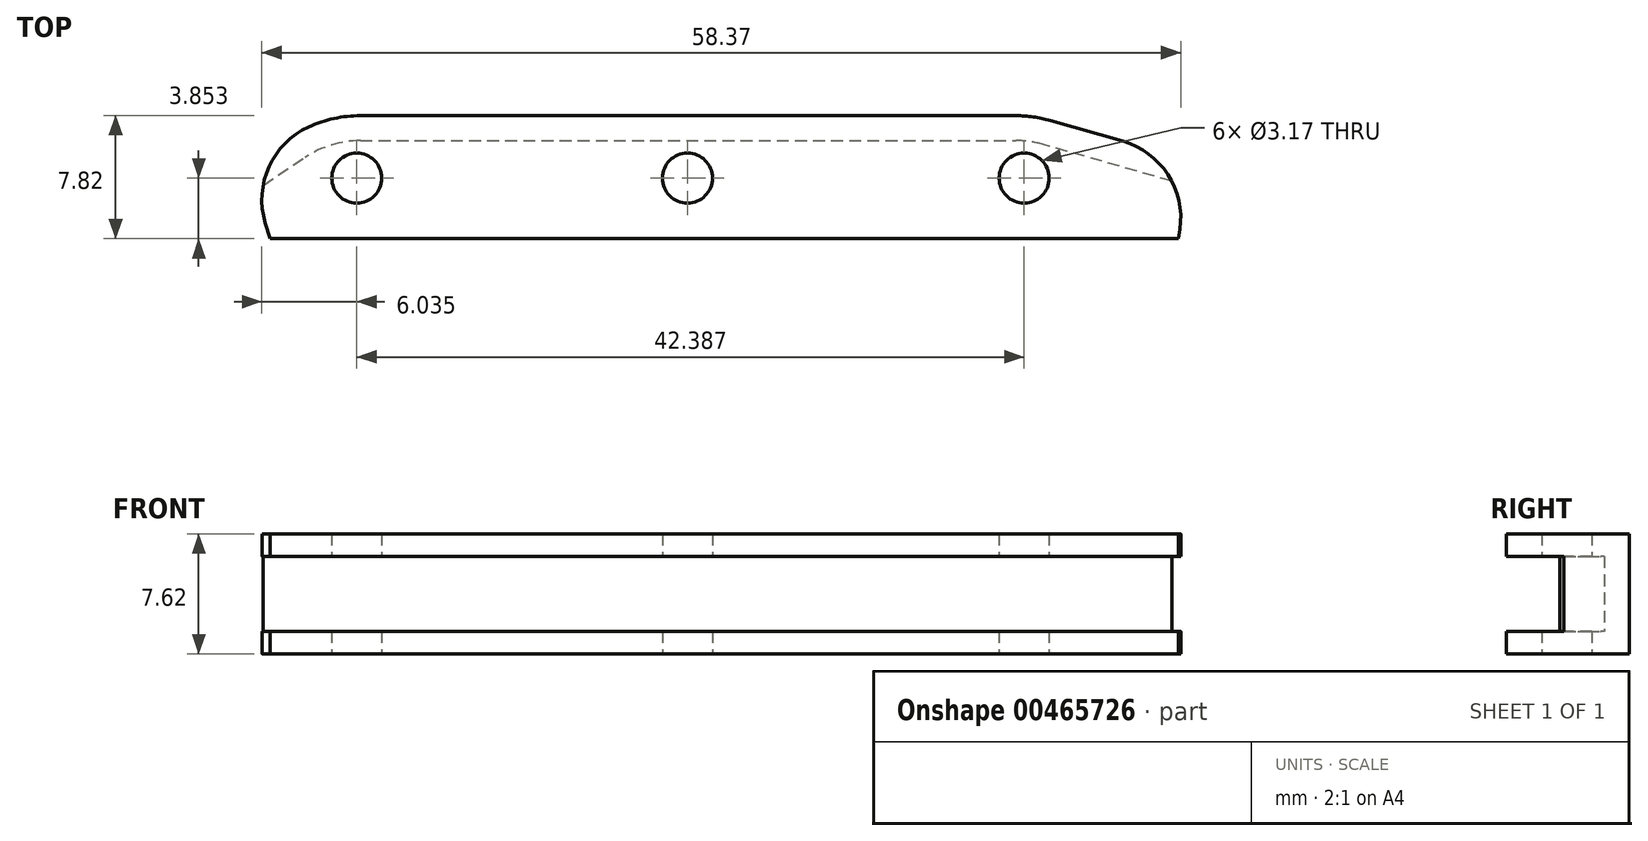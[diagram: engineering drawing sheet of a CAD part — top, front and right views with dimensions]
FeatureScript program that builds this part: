
annotation { "Feature Type Name" : "Feature", "Feature Type Description" : "" }
export const myFeature = defineFeature(function(context is Context, id is Id, definition is map)
    precondition{}
    {
        {
            var Q0;
            Q0=qCreatedBy(makeId("Front.planeOp"),FACE);
            var sketch = newSketch(context, id + "F0", { "sketchPlane" : qUnion([Q0])});
            skLineSegment(sketch, "E0", {"start": v(-32.49, -25.69) * mm, "end": v(9.15, -25.69) * mm});
            skLineSegment(sketch, "E1", {"start": v(-67.75, -3.46) * mm, "end": v(-36, -24.62) * mm});
            skLineSegment(sketch, "E2", {"start": v(87.83, -3.46) * mm, "end": v(10.9, -25.44) * mm});
            skPoint(sketch, "E3.visualSharp", {"position": v(-34.4, -25.69) * mm});
            skArc(sketch, "E3.filletArc", {"start": v(-36, -24.62) * mm, "mid": v(-34.33, -25.41) * mm, "end": v(-32.49, -25.69) * mm});
            skPoint(sketch, "E4.visualSharp", {"position": v(10.04, -25.69) * mm});
            skArc(sketch, "E4.filletArc", {"start": v(9.15, -25.69) * mm, "mid": v(10.03, -25.62) * mm, "end": v(10.9, -25.44) * mm});
            skLineSegment(sketch, "E5", {"start": v(-56.7, -19.46) * mm, "end": v(47.85, -19.46) * mm});
            skLineSegment(sketch, "E6", {"start": v(-56.7, -19.46) * mm, "end": v(-56.7, -25.69) * mm, "construction": true});
            skLineSegment(sketch, "E7.0", {"start": v(90.04, -1.93) * mm, "end": v(28.7, -19.46) * mm});
            skLineSegment(sketch, "E8.0", {"start": v(88.27, -4.99) * mm, "end": v(11.33, -26.97) * mm});
            skLineSegment(sketch, "E8.1", {"start": v(-68.63, -4.78) * mm, "end": v(-36.89, -25.94) * mm});
            skArc(sketch, "E8.2", {"start": v(-36.89, -25.94) * mm, "mid": v(-34.79, -26.93) * mm, "end": v(-32.49, -27.27) * mm});
            skLineSegment(sketch, "E8.3", {"start": v(-32.49, -27.27) * mm, "end": v(9.15, -27.27) * mm});
            skArc(sketch, "E8.4", {"start": v(9.15, -27.27) * mm, "mid": v(10.25, -27.2) * mm, "end": v(11.33, -26.97) * mm});
            skLineSegment(sketch, "E9", {"start": v(-64.74, -19.46) * mm, "end": v(55.8, -19.46) * mm, "construction": true});
            skSolve(sketch);
        }
        {
            var Q0;
            Q0=makeQuery(id+"F0.imprint","IMPRINT",FACE,{"disambiguationData":[TD([[makeQuery(id+"F0.imprint","IMPRINT",EDGE,{"derivedFrom":sQuery(id+"F0.wireOp",EDGE,"E0")}),1.0]])]});
            var Q1;
            Q1=makeQuery(id+"F0.imprint","IMPRINT",FACE,{"disambiguationData":[TD([[makeQuery(id+"F0.imprint","IMPRINT",EDGE,{"derivedFrom":sQuery(id+"F0.wireOp",EDGE,"E0")}),-1.0]])]});
            extrude(context, id + "F1", {"entities" : qUnion([Q0, Q1]), "endBound" : BoundingType.SYMMETRIC, "depth" : 7.62 * mm});
        }
        {
            var Q0;
            Q0=makeQuery(id+"F0.imprint","IMPRINT",FACE,{"disambiguationData":[TD([[makeQuery(id+"F0.imprint","IMPRINT",EDGE,{"derivedFrom":sQuery(id+"F0.wireOp",EDGE,"E0")}),1.0]])]});
            extrude(context, id + "F2", {"entities" : qUnion([Q0]), "operationType" : NewBodyOperationType.REMOVE, "endBound" : BoundingType.SYMMETRIC, "oppositeDirection" : true, "depth" : 4.76 * mm});
        }
        {
            var Q0;
            Q0=makeQuery(id+"F1.opExtrude","SWEPT_EDGE",EDGE,{"disambiguationData":[OSD([sQuery(id+"F0.wireOp",EDGE,"E5"),sQuery(id+"F0.wireOp",EDGE,"E8.1")])]});
            var Q1;
            Q1=makeQuery(id+"F1.opExtrude","SWEPT_EDGE",EDGE,{"disambiguationData":[OSD([sQuery(id+"F0.wireOp",EDGE,"E5"),sQuery(id+"F0.wireOp",EDGE,"E8.0")])]});
            chamfer(context, id + "F3", {"entities" : qUnion([Q0, Q1]), "width" : 2.54 * mm, "tangentPropagation" : true});
        }
        {
            var Q0;
            Q0=qCreatedBy(makeId("Front.planeOp"),FACE);
            var sketch = newSketch(context, id + "F4", { "sketchPlane" : qUnion([Q0])});
            skCircle(sketch, "E10", {"center": v(-32.72, -23.31) * mm, "radius": 1.59 * mm});
            skLineSegment(sketch, "E11", {"start": v(-41.05, -23.31) * mm, "end": v(31.67, -23.31) * mm, "construction": true});
            skCircle(sketch, "E12", {"center": v(9.67, -23.31) * mm, "radius": 1.59 * mm});
            skCircle(sketch, "E13", {"center": v(-11.72, -23.31) * mm, "radius": 1.59 * mm});
            skSolve(sketch);
        }
        {
            var Q0;
            Q0=makeQuery(id+"F4.imprint","IMPRINT",FACE,{"disambiguationData":[TD([[makeQuery(id+"F4.imprint","IMPRINT",EDGE,{"derivedFrom":sQuery(id+"F4.wireOp",EDGE,"E12")}),1.0]])]});
            var Q1;
            Q1=makeQuery(id+"F4.imprint","IMPRINT",FACE,{"disambiguationData":[TD([[makeQuery(id+"F4.imprint","IMPRINT",EDGE,{"derivedFrom":sQuery(id+"F4.wireOp",EDGE,"E13")}),1.0]])]});
            var Q2;
            Q2=makeQuery(id+"F4.imprint","IMPRINT",FACE,{"disambiguationData":[TD([[makeQuery(id+"F4.imprint","IMPRINT",EDGE,{"derivedFrom":sQuery(id+"F4.wireOp",EDGE,"E10")}),1.0]])]});
            extrude(context, id + "F5", {"entities" : qUnion([Q0, Q1, Q2]), "operationType" : NewBodyOperationType.REMOVE, "endBound" : BoundingType.SYMMETRIC, "oppositeDirection" : true, "depth" : 12.7 * mm});
        }
        {
            var Q0;
            {var subQ0=sQuery(id+"F0.wireOp",EDGE,"E8.1");Q0=makeQuery(id+"F3.opChamfer","BLEND_EDGE",EDGE,{"blendedFrom":[makeQuery(id+"F1.opExtrude","SWEPT_EDGE",EDGE,{"disambiguationData":[OSD([sQuery(id+"F0.wireOp",EDGE,"E5"),subQ0])]}),makeQuery(id+"F1.opExtrude","SWEPT_FACE",FACE,{"disambiguationData":[OSD([subQ0])]})],"blendedInto":[makeQuery(id+"F1.opExtrude","SWEPT_FACE",FACE,{"disambiguationData":[OSD([subQ0])]})]});}
            var Q1;
            {var subQ0=sQuery(id+"F0.wireOp",EDGE,"E8.0");Q1=makeQuery(id+"F3.opChamfer","BLEND_EDGE",EDGE,{"blendedFrom":[makeQuery(id+"F1.opExtrude","SWEPT_EDGE",EDGE,{"disambiguationData":[OSD([sQuery(id+"F0.wireOp",EDGE,"E5"),subQ0])]}),makeQuery(id+"F1.opExtrude","SWEPT_FACE",FACE,{"disambiguationData":[OSD([subQ0])]})],"blendedInto":[makeQuery(id+"F1.opExtrude","SWEPT_FACE",FACE,{"disambiguationData":[OSD([subQ0])]})]});}
            fillet(context, id + "F6", {"entities" : qUnion([Q0, Q1]), "radius" : 5.08 * mm, "tangentPropagation" : true, "allowEdgeOverflow" : false});
        }
        {
            var Q0;
            Q0=makeQuery(id+"F1.opExtrude","SWEPT_BODY",BODY,{"disambiguationData":[OSD([sQuery(id+"F0.wireOp",EDGE,"E5"),sQuery(id+"F0.wireOp",EDGE,"E8.0"),sQuery(id+"F0.wireOp",EDGE,"E8.1"),sQuery(id+"F0.wireOp",EDGE,"E8.2"),sQuery(id+"F0.wireOp",EDGE,"E8.3"),sQuery(id+"F0.wireOp",EDGE,"E8.4")])]});
            var Q1;
            Q1=sQuery(id+"F0.wireOp",EDGE,"E9");
            transform(context, id + "F7", {"entities" : qUnion([Q0]), "transformType" : TransformType.ROTATION, "transformAxis" : qUnion([Q1]), "angle" : 90 * degree, "makeCopy" : false});
        }
    });
